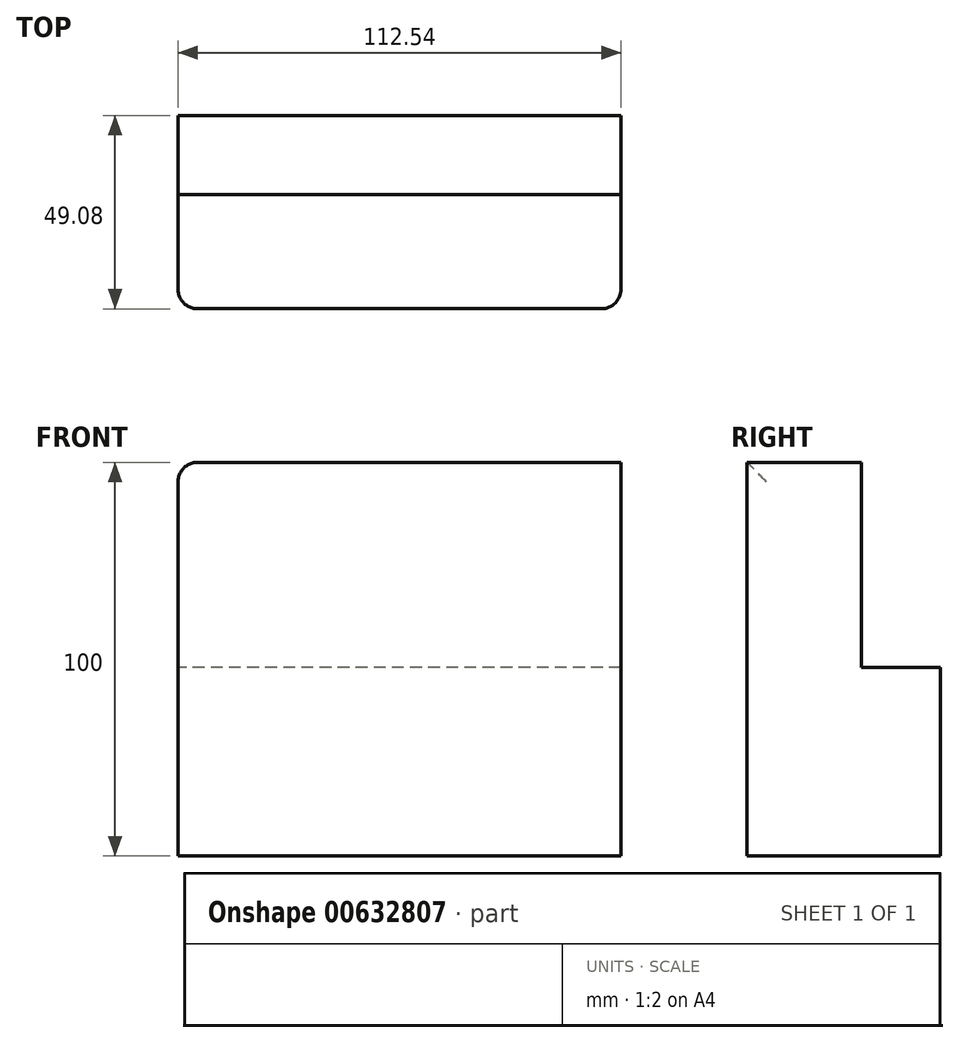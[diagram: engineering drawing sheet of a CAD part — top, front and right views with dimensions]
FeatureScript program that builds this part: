
annotation { "Feature Type Name" : "Feature", "Feature Type Description" : "" }
export const myFeature = defineFeature(function(context is Context, id is Id, definition is map)
    precondition{}
    {
        {
            var Q0;
            Q0=qCreatedBy(makeId("Top.planeOp"),FACE);
            var sketch = newSketch(context, id + "F0", { "sketchPlane" : qUnion([Q0])});
            skLineSegment(sketch, "E0.bottom", {"start": v(56.27, -24.54) * mm, "end": v(-56.27, -24.54) * mm});
            skLineSegment(sketch, "E0.top", {"start": v(56.27, 24.54) * mm, "end": v(-56.27, 24.54) * mm});
            skLineSegment(sketch, "E0.left", {"start": v(56.27, -24.54) * mm, "end": v(56.27, 24.54) * mm});
            skLineSegment(sketch, "E0.right", {"start": v(-56.27, -24.54) * mm, "end": v(-56.27, 24.54) * mm});
            skPoint(sketch, "E0.middle", {"position": v(0, 0) * mm});
            skSolve(sketch);
        }
        {
            var Q0;
            Q0=makeQuery(id+"F0.imprint","IMPRINT",FACE,{"disambiguationData":[TD([[makeQuery(id+"F0.imprint","IMPRINT",EDGE,{"derivedFrom":sQuery(id+"F0.wireOp",EDGE,"E0.bottom")}),-1.0]])]});
            extrude(context, id + "F1", {"entities" : qUnion([Q0]), "depth" : 50 * mm, "offsetDistance" : 25 * mm});
        }
        {
            var Q0;
            Q0=makeQuery(id+"F1.opExtrude","CAP_FACE",FACE,{"disambiguationData":[OSD([sQuery(id+"F0.wireOp",EDGE,"E0.bottom"),sQuery(id+"F0.wireOp",EDGE,"E0.top"),sQuery(id+"F0.wireOp",EDGE,"E0.left"),sQuery(id+"F0.wireOp",EDGE,"E0.right")])],"isStart":true});
            extrude(context, id + "F2", {"entities" : qUnion([Q0]), "operationType" : NewBodyOperationType.ADD, "depth" : 50 * mm, "offsetDistance" : 25 * mm});
        }
        {
            var Q0;
            {var subQ0=sQuery(id+"F0.wireOp",EDGE,"E0.top");Q0=makeQuery(id+"F2.boolean.opBoolean","MERGE",FACE,{"derivedFrom":[makeQuery(id+"F1.opExtrude","SWEPT_FACE",FACE,{"disambiguationData":[OSD([subQ0])]}),makeQuery(id+"F2.opExtrude","SWEPT_FACE",FACE,{"disambiguationData":[OSD([subQ0])]})]});}
            var sketch = newSketch(context, id + "F3", { "sketchPlane" : qUnion([Q0])});
            skLineSegment(sketch, "E1", {"start": v(-56.27, 3.26) * mm, "end": v(56.27, 3.26) * mm});
            skLineSegment(sketch, "E2", {"start": v(-56.27, -2.12) * mm, "end": v(56.27, -2.12) * mm});
            skSolve(sketch);
        }
        {
            var Q0;
            {var subQ0=sQuery(id+"F3.wireOp",EDGE,"E1");Q0=makeQuery(id+"F3.imprint","IMPRINT",FACE,{"disambiguationData":[TD([[makeQuery(id+"F3.imprint","IMPRINT",EDGE,{"derivedFrom":subQ0}),-1.0]])]});}
            var Q1;
            {var subQ0=sQuery(id+"F3.wireOp",EDGE,"E1");Q1=makeQuery(id+"F3.imprint","IMPRINT",FACE,{"disambiguationData":[TD([[makeQuery(id+"F3.imprint","IMPRINT",EDGE,{"derivedFrom":subQ0}),1.0]])]});}
            extrude(context, id + "F4", {"entities" : qUnion([Q0, Q1]), "operationType" : NewBodyOperationType.REMOVE, "oppositeDirection" : true, "depth" : 20 * mm, "offsetDistance" : 25 * mm});
        }
        {
            var Q0;
            Q0=makeQuery(id+"F4.boolean.opBoolean","COPY",EDGE,{"derivedFrom":makeQuery(id+"F4.opExtrude","CAP_EDGE",EDGE,{"disambiguationData":[OSD([sQuery(id+"F0.wireOp",EDGE,"E0.top")])],"isStart":false})});
            var Q1;
            Q1=makeQuery(id+"F1.opExtrude","CAP_EDGE",EDGE,{"disambiguationData":[OSD([sQuery(id+"F0.wireOp",EDGE,"E0.right")])],"isStart":false});
            var Q2;
            {var subQ0=sQuery(id+"F0.wireOp",EDGE,"E0.left");var subQ1=sQuery(id+"F0.wireOp",EDGE,"E0.bottom");Q2=makeQuery(id+"F2.boolean.opBoolean","MERGE",EDGE,{"derivedFrom":[makeQuery(id+"F1.opExtrude","SWEPT_EDGE",EDGE,{"disambiguationData":[OSD([subQ1,subQ0])]}),makeQuery(id+"F2.opExtrude","SWEPT_EDGE",EDGE,{"disambiguationData":[OSD([subQ1,subQ0])]})]});}
            var Q3;
            {var subQ0=sQuery(id+"F0.wireOp",EDGE,"E0.right");var subQ1=sQuery(id+"F0.wireOp",EDGE,"E0.bottom");Q3=makeQuery(id+"F2.boolean.opBoolean","MERGE",EDGE,{"derivedFrom":[makeQuery(id+"F1.opExtrude","SWEPT_EDGE",EDGE,{"disambiguationData":[OSD([subQ1,subQ0])]}),makeQuery(id+"F2.opExtrude","SWEPT_EDGE",EDGE,{"disambiguationData":[OSD([subQ1,subQ0])]})]});}
            fillet(context, id + "F5", {"entities" : qUnion([Q0, Q1, Q2, Q3]), "radius" : 5 * mm, "tangentPropagation" : true, "allowEdgeOverflow" : false});
        }
    });
